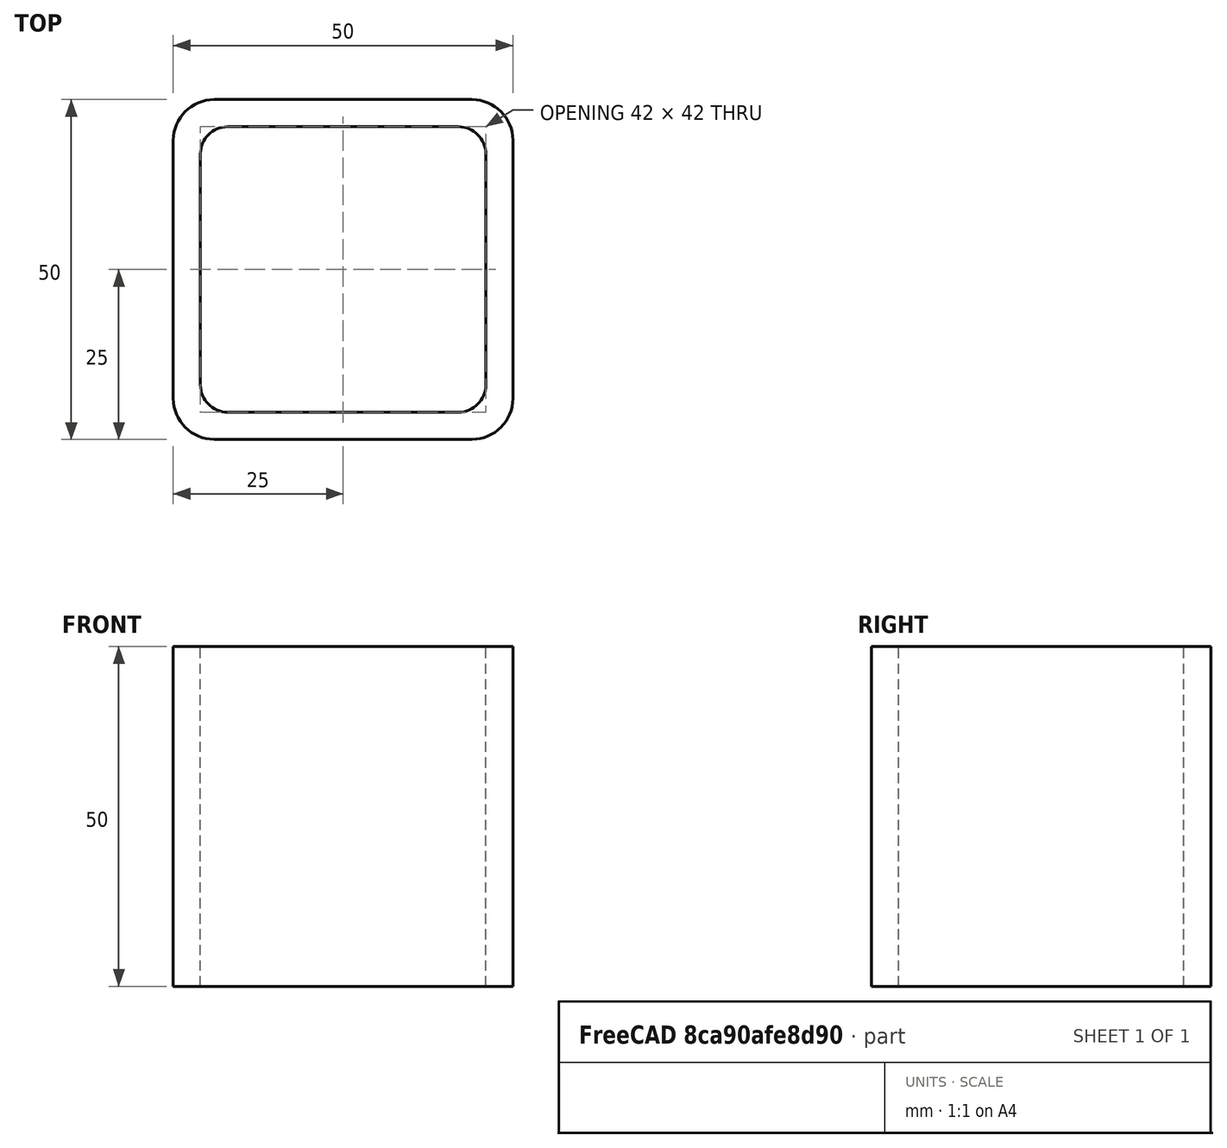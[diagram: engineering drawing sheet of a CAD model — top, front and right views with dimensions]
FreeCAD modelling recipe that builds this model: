
FCSTD DOCUMENT  (FreeCAD 0.15R4671 (Git))
Label: Square hollow section 50x50x4 EN10219 S235JRH
License: All rights reserved
LicenseURL: http://en.wikipedia.org/wiki/All_rights_reserved
objects: Sketcher::SketchObject×1, Part::Extrusion×1
note: 2 computed .brp shape members not serialized (recipe doc carries the construction recipe); baked Part::Feature solids carry a one-line shape summary decoded from their .brp

FEATURE [Sketcher::SketchObject] Sketch
  sketch-geometry (16):
    g0: LineSegment StartX=-17 StartY=21 StartZ=0 EndX=17 EndY=21 EndZ=0
    g1: LineSegment StartX=21 StartY=17 StartZ=0 EndX=21 EndY=-17 EndZ=0
    g2: LineSegment StartX=17 StartY=-21 StartZ=0 EndX=-17 EndY=-21 EndZ=0
    g3: LineSegment StartX=-21 StartY=-17 StartZ=0 EndX=-21 EndY=17 EndZ=0
    g4: LineSegment StartX=-19 StartY=25 StartZ=0 EndX=19 EndY=25 EndZ=0
    g5: LineSegment StartX=25 StartY=19 StartZ=0 EndX=25 EndY=-19 EndZ=0
    g6: LineSegment StartX=19 StartY=-25 StartZ=0 EndX=-19 EndY=-25 EndZ=0
    g7: LineSegment StartX=-25 StartY=-19 StartZ=0 EndX=-25 EndY=19 EndZ=0
    g8: ArcOfCircle CenterX=-17 CenterY=17 CenterZ=0 NormalX=0 NormalY=0 NormalZ=1 Radius=4 StartAngle=1.5708 EndAngle=3.14159
    g9: ArcOfCircle CenterX=17 CenterY=17 CenterZ=0 NormalX=0 NormalY=0 NormalZ=1 Radius=4 StartAngle=0 EndAngle=1.5708
    g10: ArcOfCircle CenterX=17 CenterY=-17 CenterZ=0 NormalX=0 NormalY=0 NormalZ=1 Radius=4 StartAngle=4.71239 EndAngle=6.28319
    g11: ArcOfCircle CenterX=-17 CenterY=-17 CenterZ=0 NormalX=0 NormalY=0 NormalZ=1 Radius=4 StartAngle=3.14159 EndAngle=4.71239
    g12: ArcOfCircle CenterX=19 CenterY=19 CenterZ=0 NormalX=0 NormalY=0 NormalZ=1 Radius=6 StartAngle=0 EndAngle=1.5708
    g13: ArcOfCircle CenterX=19 CenterY=-19 CenterZ=0 NormalX=0 NormalY=0 NormalZ=1 Radius=6 StartAngle=4.71239 EndAngle=6.28319
    g14: ArcOfCircle CenterX=-19 CenterY=-19 CenterZ=0 NormalX=0 NormalY=0 NormalZ=1 Radius=6 StartAngle=3.14159 EndAngle=4.71239
    g15: ArcOfCircle CenterX=-19 CenterY=19 CenterZ=0 NormalX=0 NormalY=0 NormalZ=1 Radius=6 StartAngle=1.5708 EndAngle=3.14159
  constraints (36):
    c: Horizontal(g2)
    c: Vertical(g3)
    c: Horizontal(g6)
    c: Vertical(g7)
    c: Tangent(g3,g8) = 1.5708
    c: Tangent(g0,g8) = 1.5708
    c: Tangent(g0,g9) = 1.5708
    c: Tangent(g1,g9) = 1.5708
    c: Tangent(g1,g10) = 1.5708
    c: Tangent(g2,g10) = 1.5708
    c: Tangent(g2,g11) = 1.5708
    c: Tangent(g3,g11) = 1.5708
    c: Tangent(g4,g12) = 1.5708
    c: Tangent(g5,g12) = 1.5708
    c: Tangent(g5,g13) = 1.5708
    c: Tangent(g6,g13) = 1.5708
    c: Tangent(g6,g14) = 1.5708
    c: Tangent(g7,g14) = 1.5708
    c: Tangent(g7,g15) = 1.5708
    c: Tangent(g4,g15) = 1.5708
    c: Equal(g9,g8)
    c: Equal(g9,g11)
    c: Equal(g9,g10)
    c: Equal(g12,g15)
    c: Equal(g12,g14)
    c: Equal(g12,g13)
    c: Symmetric(g4,g6,g-1)
    c: Symmetric(g7,g5,g-2)
    c: DistanceY(g4,g6) = -50
    c: DistanceX(g7,g5) = 50
    c: Symmetric(g3,g1,g-2)
    c: Symmetric(g0,g2,g-1)
    c: DistanceY(g0,g4) = 4
    c: DistanceX(g5,g1) = -4
    c: Radius(g9) = 4
    c: Radius(g12) = 6
FEATURE [Part::Extrusion] Extrude  label="Square hollow section 50x50x4 EN10219 S235JRH"
  Base = -> Sketch
  Dir = (0,0,50)
  Solid = true
